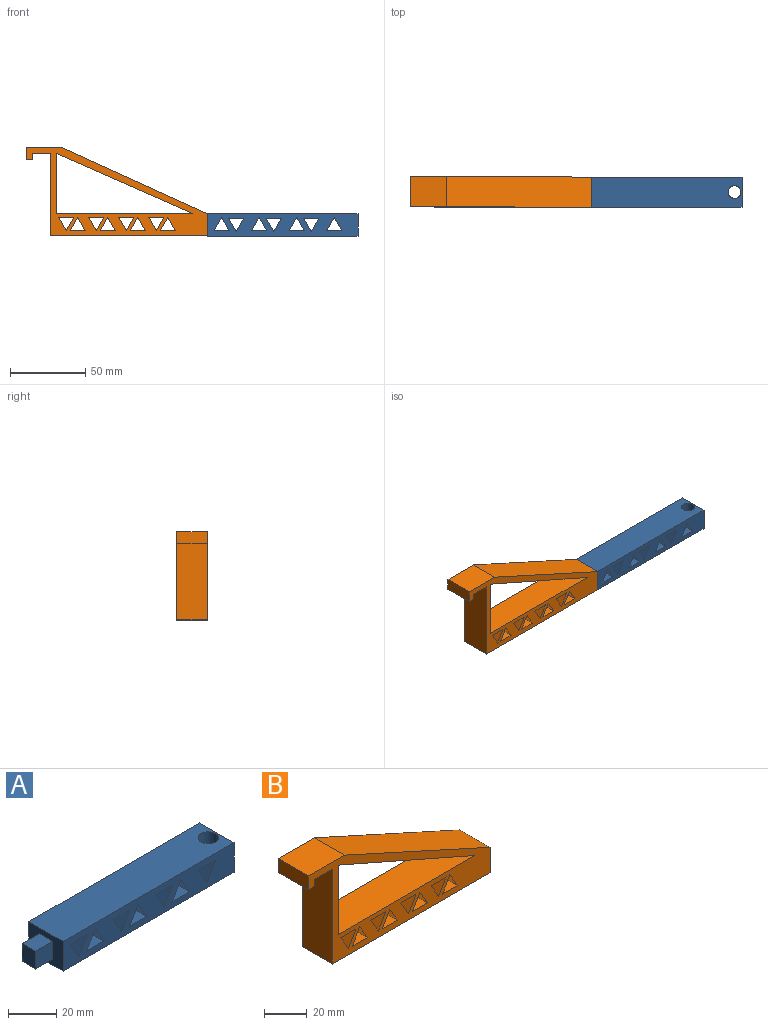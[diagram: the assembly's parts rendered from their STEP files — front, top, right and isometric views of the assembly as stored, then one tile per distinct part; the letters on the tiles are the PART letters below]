
ASSEMBLY  parts=2 mates=1
PART A: 33 faces, bbox 110x20x15 mm
  f0: plane 20x15mm, normal (-1,0,0), area 228mm2, adj f1,f2,f4,f5,f6,f7,f8,f9
  f1: plane 100x20mm, normal (0,0,1), area 1943.3mm2, adj f0,f3,f4,f5,f32
  f2: plane 100x20mm, normal (0,0,-1), area 1943.3mm2, adj f0,f3,f4,f5,f32
  f3: plane 20x15mm, normal (1,0,0), area 300mm2, adj f1,f2,f4,f5
  f4: plane 100x15mm, normal (0,1,0), area 1196.9mm2, adj f0,f1,f2,f3,f11,f12,f13,f14
  f5: plane 100x15mm, normal (0,-1,0), area 1196.9mm2, adj f0,f1,f2,f3,f11,f12,f13,f14
  f6: plane 10x8mm, normal (0,0,-1), area 80mm2, adj f0,f7,f9,f10
  f7: plane 10x9mm, normal (0,-1,0), area 90mm2, adj f0,f6,f8,f10
  f8: plane 10x8mm, normal (0,0,1), area 80mm2, adj f0,f7,f9,f10
  f9: plane 10x9mm, normal (0,1,0), area 90mm2, adj f0,f6,f8,f10
  f10: plane 9x8mm, normal (-1,0,0), area 72mm2, adj f6,f7,f8,f9
  f11: plane 20x8.66mm, normal (0.87,0,0.5), area 200mm2, adj f4,f5,f12,f13
  f12: plane 20x8.66mm, normal (-0.87,0,0.5), area 200mm2, adj f4,f5,f11,f13
  f13: plane 20x10mm, normal (0,0,-1), area 200mm2, adj f4,f5,f11,f12
  f14: plane 20x8.66mm, normal (0.87,0,0.5), area 200mm2, adj f4,f5,f15,f16
  f15: plane 20x8.66mm, normal (-0.87,0,0.5), area 200mm2, adj f4,f5,f14,f16
  f16: plane 20x10mm, normal (0,0,-1), area 200mm2, adj f4,f5,f14,f15
  f17: plane 20x8.66mm, normal (0.87,0,-0.5), area 200mm2, adj f4,f5,f18,f19
  f18: plane 20x10mm, normal (0,0,1), area 200mm2, adj f4,f5,f17,f19
  f19: plane 20x8.66mm, normal (-0.87,0,-0.5), area 200mm2, adj f4,f5,f17,f18
  f20: plane 20x8.66mm, normal (0.87,0,-0.5), area 200mm2, adj f4,f5,f21,f22
  f21: plane 20x10mm, normal (0,0,1), area 200mm2, adj f4,f5,f20,f22
  f22: plane 20x8.66mm, normal (-0.87,0,-0.5), area 200mm2, adj f4,f5,f20,f21
  f23: plane 20x8.66mm, normal (0.87,0,0.5), area 200mm2, adj f4,f5,f24,f25
  f24: plane 20x8.66mm, normal (-0.87,0,0.5), area 200mm2, adj f4,f5,f23,f25
  f25: plane 20x10mm, normal (0,0,-1), area 200mm2, adj f4,f5,f23,f24
  f26: plane 20x8.66mm, normal (0.87,0,-0.5), area 200mm2, adj f4,f5,f27,f28
  f27: plane 20x10mm, normal (0,0,1), area 200mm2, adj f4,f5,f26,f28
  f28: plane 20x8.66mm, normal (-0.87,0,-0.5), area 200mm2, adj f4,f5,f26,f27
  f29: plane 20x8.66mm, normal (0.87,0,0.5), area 200mm2, adj f4,f5,f30,f31
  f30: plane 20x8.66mm, normal (-0.87,0,0.5), area 200mm2, adj f4,f5,f29,f31
  f31: plane 20x10mm, normal (0,0,-1), area 200mm2, adj f4,f5,f29,f30
  f32: cylinder r=4.25mm len=15mm, axis (0,0,1), area 400.6mm2, adj f1,f2
PART B: 43 faces, bbox 121x20x58.7 mm
  f0: plane 20x14.72mm, normal (1,0,0), area 224.7mm2, adj f8,f9,f12,f13,f38,f39,f40,f41
  f1: plane 40x20mm, normal (1,0,0), area 800mm2, adj f2,f11,f12,f13
  f2: plane 91.02x40mm, normal (-0.4,0,-0.92), area 1988.3mm2, adj f1,f11,f12,f13
  f3: plane 20x8mm, normal (-1,0,0), area 160mm2, adj f4,f10,f12,f13
  f4: plane 20x4mm, normal (0,0,-1), area 80mm2, adj f3,f5,f12,f13
  f5: plane 20x4mm, normal (1,0,0), area 80mm2, adj f4,f6,f12,f13
  f6: plane 20x12mm, normal (0,0,-1), area 240mm2, adj f5,f7,f12,f13
  f7: plane 54.71x20mm, normal (-1,0,0), area 1094.3mm2, adj f6,f8,f12,f13
  f8: plane 105x20mm, normal (0,0,-1), area 2100mm2, adj f0,f7,f12,f13
  f9: plane 97x43.99mm, normal (0.41,0,0.91), area 2130.2mm2, adj f0,f10,f12,f13
  f10: plane 24x20mm, normal (0,0,1), area 480mm2, adj f3,f9,f12,f13
  f11: plane 91.02x20mm, normal (0,0,1), area 1820.3mm2, adj f1,f2,f12,f13
  f12: plane 121x58.71mm, normal (0,1,0), area 1944.7mm2, adj f0,f1,f2,f3,f4,f5,f6,f7
  f13: plane 121x58.71mm, normal (0,-1,0), area 1944.7mm2, adj f0,f1,f2,f3,f4,f5,f6,f7
  f14: plane 20x8.66mm, normal (-0.87,0,0.5), area 200mm2, adj f12,f13,f15,f16
  f15: plane 20x10mm, normal (0,0,-1), area 200mm2, adj f12,f13,f14,f16
  f16: plane 20x8.66mm, normal (0.87,0,0.5), area 200mm2, adj f12,f13,f14,f15
  f17: plane 20x8.66mm, normal (-0.87,0,0.5), area 200mm2, adj f12,f13,f18,f19
  f18: plane 20x10mm, normal (0,0,-1), area 200mm2, adj f12,f13,f17,f19
  f19: plane 20x8.66mm, normal (0.87,0,0.5), area 200mm2, adj f12,f13,f17,f18
  f20: plane 20x8.66mm, normal (-0.87,0,0.5), area 200mm2, adj f12,f13,f21,f22
  f21: plane 20x10mm, normal (0,0,-1), area 200mm2, adj f12,f13,f20,f22
  f22: plane 20x8.66mm, normal (0.87,0,0.5), area 200mm2, adj f12,f13,f20,f21
  f23: plane 20x8.66mm, normal (-0.87,0,-0.5), area 200mm2, adj f12,f13,f24,f25
  f24: plane 20x8.66mm, normal (0.87,0,-0.5), area 200mm2, adj f12,f13,f23,f25
  f25: plane 20x10mm, normal (0,0,1), area 200mm2, adj f12,f13,f23,f24
  f26: plane 20x8.66mm, normal (-0.87,0,-0.5), area 200mm2, adj f12,f13,f27,f28
  f27: plane 20x8.66mm, normal (0.87,0,-0.5), area 200mm2, adj f12,f13,f26,f28
  f28: plane 20x10mm, normal (0,0,1), area 200mm2, adj f12,f13,f26,f27
  f29: plane 20x8.66mm, normal (-0.87,0,0.5), area 200mm2, adj f12,f13,f30,f31
  f30: plane 20x10mm, normal (0,0,-1), area 200mm2, adj f12,f13,f29,f31
  f31: plane 20x8.66mm, normal (0.87,0,0.5), area 200mm2, adj f12,f13,f29,f30
  f32: plane 20x8.66mm, normal (-0.87,0,-0.5), area 200mm2, adj f12,f13,f33,f34
  f33: plane 20x8.66mm, normal (0.87,0,-0.5), area 200mm2, adj f12,f13,f32,f34
  f34: plane 20x10mm, normal (0,0,1), area 200mm2, adj f12,f13,f32,f33
  f35: plane 20x8.66mm, normal (-0.87,0,-0.5), area 200mm2, adj f12,f13,f36,f37
  f36: plane 20x8.66mm, normal (0.87,0,-0.5), area 200mm2, adj f12,f13,f35,f37
  f37: plane 20x10mm, normal (0,0,1), area 200mm2, adj f12,f13,f35,f36
  f38: plane 10x8mm, normal (0,0,-1), area 80mm2, adj f0,f39,f41,f42
  f39: plane 10x8.72mm, normal (0,1,0), area 87.2mm2, adj f0,f38,f40,f42
  f40: plane 10x8mm, normal (0,0,1), area 80mm2, adj f0,f39,f41,f42
  f41: plane 10x8.72mm, normal (0,-1,0), area 87.2mm2, adj f0,f38,f40,f42
  f42: plane 8.72x8mm, normal (1,0,0), area 69.8mm2, adj f38,f39,f40,f41
PLACE A rot(axis=(1,0,0),180deg) t=(89,20,-18.74)mm
PLACE B at identity fixed
MATE fastened B.f0 <-> A.f0  axis (1,0,0) through (66.67,10,14.01)mm
